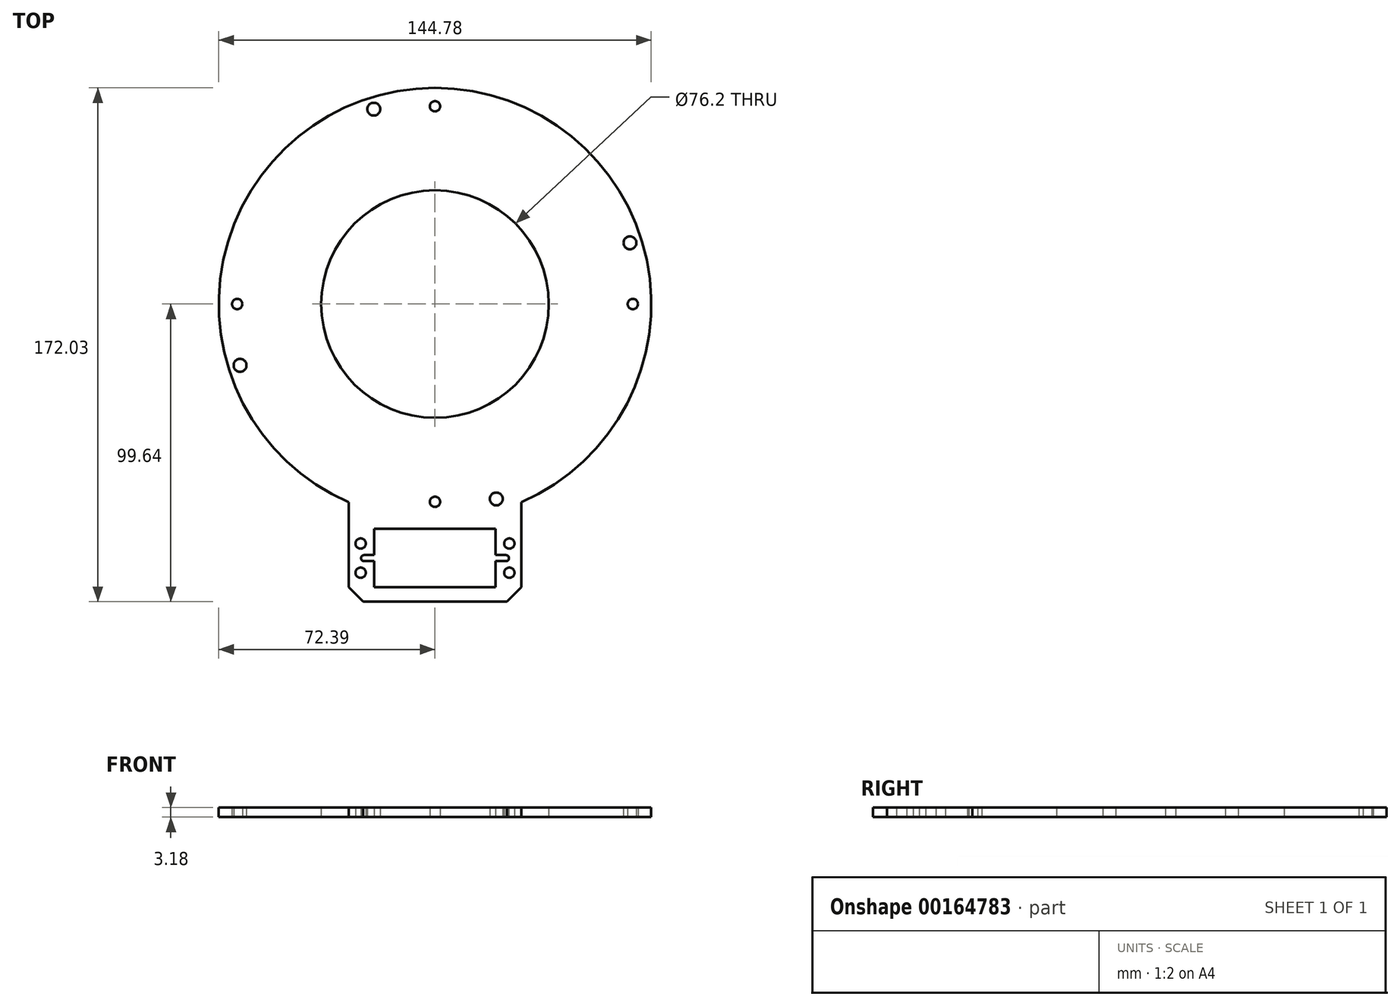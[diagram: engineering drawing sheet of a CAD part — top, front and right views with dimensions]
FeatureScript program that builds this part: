
annotation { "Feature Type Name" : "Feature", "Feature Type Description" : "" }
export const myFeature = defineFeature(function(context is Context, id is Id, definition is map)
    precondition{}
    {
        {
            var Q0;
            Q0=qCreatedBy(makeId("Top.planeOp"),FACE);
            var sketch = newSketch(context, id + "F0", { "sketchPlane" : qUnion([Q0])});
            skLineSegment(sketch, "E0.bottom", {"start": v(65.27, 20.51) * mm, "end": v(-20.51, 65.27) * mm, "construction": true});
            skLineSegment(sketch, "E0.top", {"start": v(20.51, -65.27) * mm, "end": v(-65.27, -20.51) * mm, "construction": true});
            skLineSegment(sketch, "E0.left", {"start": v(65.27, 20.51) * mm, "end": v(20.51, -65.27) * mm, "construction": true});
            skLineSegment(sketch, "E0.right", {"start": v(-20.51, 65.27) * mm, "end": v(-65.27, -20.51) * mm, "construction": true});
            skPoint(sketch, "E0.middle", {"position": v(0, 0) * mm});
            skCircle(sketch, "E1", {"center": v(65.27, 20.51) * mm, "radius": 3.97 * mm, "construction": true});
            skCircle(sketch, "E2", {"center": v(-20.51, 65.27) * mm, "radius": 2.15 * mm});
            skCircle(sketch, "E3", {"center": v(-65.27, -20.51) * mm, "radius": 2.15 * mm});
            skCircle(sketch, "E4", {"center": v(20.51, -65.27) * mm, "radius": 2.15 * mm});
            skCircle(sketch, "E5", {"center": v(65.27, 20.51) * mm, "radius": 2.15 * mm});
            skLineSegment(sketch, "E6.bottom", {"start": v(66.23, 0) * mm, "end": v(0, -66.23) * mm, "construction": true});
            skLineSegment(sketch, "E6.top", {"start": v(0, 66.23) * mm, "end": v(-66.23, 0) * mm, "construction": true});
            skLineSegment(sketch, "E6.left", {"start": v(66.23, 0) * mm, "end": v(0, 66.23) * mm, "construction": true});
            skLineSegment(sketch, "E6.right", {"start": v(0, -66.23) * mm, "end": v(-66.23, 0) * mm, "construction": true});
            skCircle(sketch, "E7", {"center": v(-66.23, 0) * mm, "radius": 1.73 * mm});
            skCircle(sketch, "E8", {"center": v(0, 66.23) * mm, "radius": 1.73 * mm});
            skCircle(sketch, "E9", {"center": v(66.23, 0) * mm, "radius": 1.73 * mm});
            skCircle(sketch, "E10", {"center": v(0, -66.23) * mm, "radius": 1.73 * mm});
            skLineSegment(sketch, "E11", {"start": v(0, 0) * mm, "end": v(0, -66.23) * mm, "construction": true});
            skLineSegment(sketch, "E12", {"start": v(0, 0) * mm, "end": v(-22.38, -42.9) * mm, "construction": true});
            skCircle(sketch, "E13", {"center": v(0, 0) * mm, "radius": 38.1 * mm});
            skLineSegment(sketch, "E14.bottom", {"start": v(24.9, -89.98) * mm, "end": v(-24.9, -89.98) * mm, "construction": true});
            skLineSegment(sketch, "E14.top", {"start": v(24.9, -80.2) * mm, "end": v(-24.9, -80.2) * mm, "construction": true});
            skLineSegment(sketch, "E14.left", {"start": v(24.9, -89.98) * mm, "end": v(24.9, -80.2) * mm, "construction": true});
            skLineSegment(sketch, "E14.right", {"start": v(-24.9, -89.98) * mm, "end": v(-24.9, -80.2) * mm, "construction": true});
            skPoint(sketch, "E14.middle", {"position": v(0, -85.1) * mm});
            skCircle(sketch, "E15", {"center": v(-24.9, -89.98) * mm, "radius": 1.73 * mm});
            skCircle(sketch, "E16", {"center": v(-24.9, -80.2) * mm, "radius": 1.73 * mm});
            skCircle(sketch, "E17", {"center": v(24.9, -80.2) * mm, "radius": 1.73 * mm});
            skCircle(sketch, "E18", {"center": v(24.9, -89.98) * mm, "radius": 1.73 * mm});
            skLineSegment(sketch, "E19.bottom", {"start": v(-20.32, -86.11) * mm, "end": v(-23.75, -86.11) * mm});
            skLineSegment(sketch, "E19.top", {"start": v(-20.32, -84.08) * mm, "end": v(-23.75, -84.08) * mm});
            skLineSegment(sketch, "E19.left", {"start": v(-23.75, -86.11) * mm, "end": v(-23.75, -84.08) * mm, "construction": true});
            skLineSegment(sketch, "E19.right", {"start": v(-20.32, -86.11) * mm, "end": v(-20.32, -84.08) * mm, "construction": true});
            skLineSegment(sketch, "E20.bottom", {"start": v(20.32, -86.11) * mm, "end": v(23.75, -86.11) * mm});
            skLineSegment(sketch, "E20.top", {"start": v(20.32, -84.08) * mm, "end": v(23.75, -84.08) * mm});
            skLineSegment(sketch, "E20.left", {"start": v(20.32, -86.11) * mm, "end": v(20.32, -84.08) * mm, "construction": true});
            skLineSegment(sketch, "E20.right", {"start": v(23.75, -86.11) * mm, "end": v(23.75, -84.08) * mm, "construction": true});
            skArc(sketch, "E21", {"start": v(-23.75, -84.08) * mm, "mid": v(-24.77, -85.1) * mm, "end": v(-23.75, -86.11) * mm});
            skArc(sketch, "E22", {"start": v(23.75, -86.11) * mm, "mid": v(24.77, -85.1) * mm, "end": v(23.75, -84.08) * mm});
            skLineSegment(sketch, "E23", {"start": v(-20.32, -86.11) * mm, "end": v(-20.32, -94.87) * mm});
            skLineSegment(sketch, "E24", {"start": v(-20.32, -94.87) * mm, "end": v(20.32, -94.87) * mm});
            skLineSegment(sketch, "E25", {"start": v(20.32, -94.87) * mm, "end": v(20.32, -86.11) * mm});
            skLineSegment(sketch, "E26", {"start": v(-20.32, -84.08) * mm, "end": v(-20.32, -75.32) * mm});
            skLineSegment(sketch, "E27", {"start": v(-20.32, -75.32) * mm, "end": v(20.32, -75.32) * mm});
            skLineSegment(sketch, "E28", {"start": v(20.32, -75.32) * mm, "end": v(20.32, -84.08) * mm});
            skLineSegment(sketch, "E29", {"start": v(0, -75.32) * mm, "end": v(0, -94.87) * mm, "construction": true});
            skLineSegment(sketch, "E30", {"start": v(-20.32, -85.1) * mm, "end": v(-10.9, -85.1) * mm, "construction": true});
            skArc(sketch, "E31", {"start": v(28.86, -66.39) * mm, "mid": v(0, 72.4) * mm, "end": v(-28.86, -66.39) * mm});
            skLineSegment(sketch, "E32", {"start": v(-28.86, -66.39) * mm, "end": v(-28.86, -99.64) * mm});
            skLineSegment(sketch, "E33", {"start": v(-28.86, -99.64) * mm, "end": v(28.86, -99.64) * mm});
            skLineSegment(sketch, "E34", {"start": v(28.86, -99.64) * mm, "end": v(28.86, -66.39) * mm});
            skLineSegment(sketch, "E35", {"start": v(-24.9, -85.1) * mm, "end": v(-28.86, -85.1) * mm, "construction": true});
            skLineSegment(sketch, "E36", {"start": v(0, -94.87) * mm, "end": v(0, -99.64) * mm, "construction": true});
            skCircle(sketch, "E37", {"center": v(0, 0) * mm, "radius": 71.41 * mm, "construction": true});
            skCircle(sketch, "E38", {"center": v(-10.9, -85.1) * mm, "radius": 14.38 * mm, "construction": true});
            skArc(sketch, "E39", {"start": v(-28.86, -66.39) * mm, "mid": v(0, -72.4) * mm, "end": v(28.86, -66.39) * mm, "construction": true});
            skSolve(sketch);
        }
        {
            var Q0;
            Q0=makeQuery(id+"F0.imprint","IMPRINT",FACE,{"disambiguationData":[TD([[makeQuery(id+"F0.imprint","IMPRINT",EDGE,{"derivedFrom":sQuery(id+"F0.wireOp",EDGE,"zkLWj6W1-boE5-zS3n-Wg77-nrDD3k1jm4QZ")}),1.0]])]});
            var Q1;
            Q1=makeQuery(id+"F0.imprint","IMPRINT",FACE,{"disambiguationData":[TD([[makeQuery(id+"F0.imprint","IMPRINT",EDGE,{"derivedFrom":sQuery(id+"F0.wireOp",EDGE,"E2")}),-1.0]])]});
            extrude(context, id + "F1", {"entities" : qUnion([Q0, Q1]), "depth" : 3.17 * mm});
        }
        {
            var Q0;
            Q0=makeQuery(id+"F1.opExtrude","SWEPT_EDGE",EDGE,{"disambiguationData":[OSD([sQuery(id+"F0.wireOp",EDGE,"E32"),sQuery(id+"F0.wireOp",EDGE,"E33")])]});
            var Q1;
            Q1=makeQuery(id+"F1.opExtrude","SWEPT_EDGE",EDGE,{"disambiguationData":[OSD([sQuery(id+"F0.wireOp",EDGE,"E33"),sQuery(id+"F0.wireOp",EDGE,"E34")])]});
            chamfer(context, id + "F2", {"entities" : qUnion([Q0, Q1]), "width" : 4.76 * mm, "tangentPropagation" : true});
        }
    });
